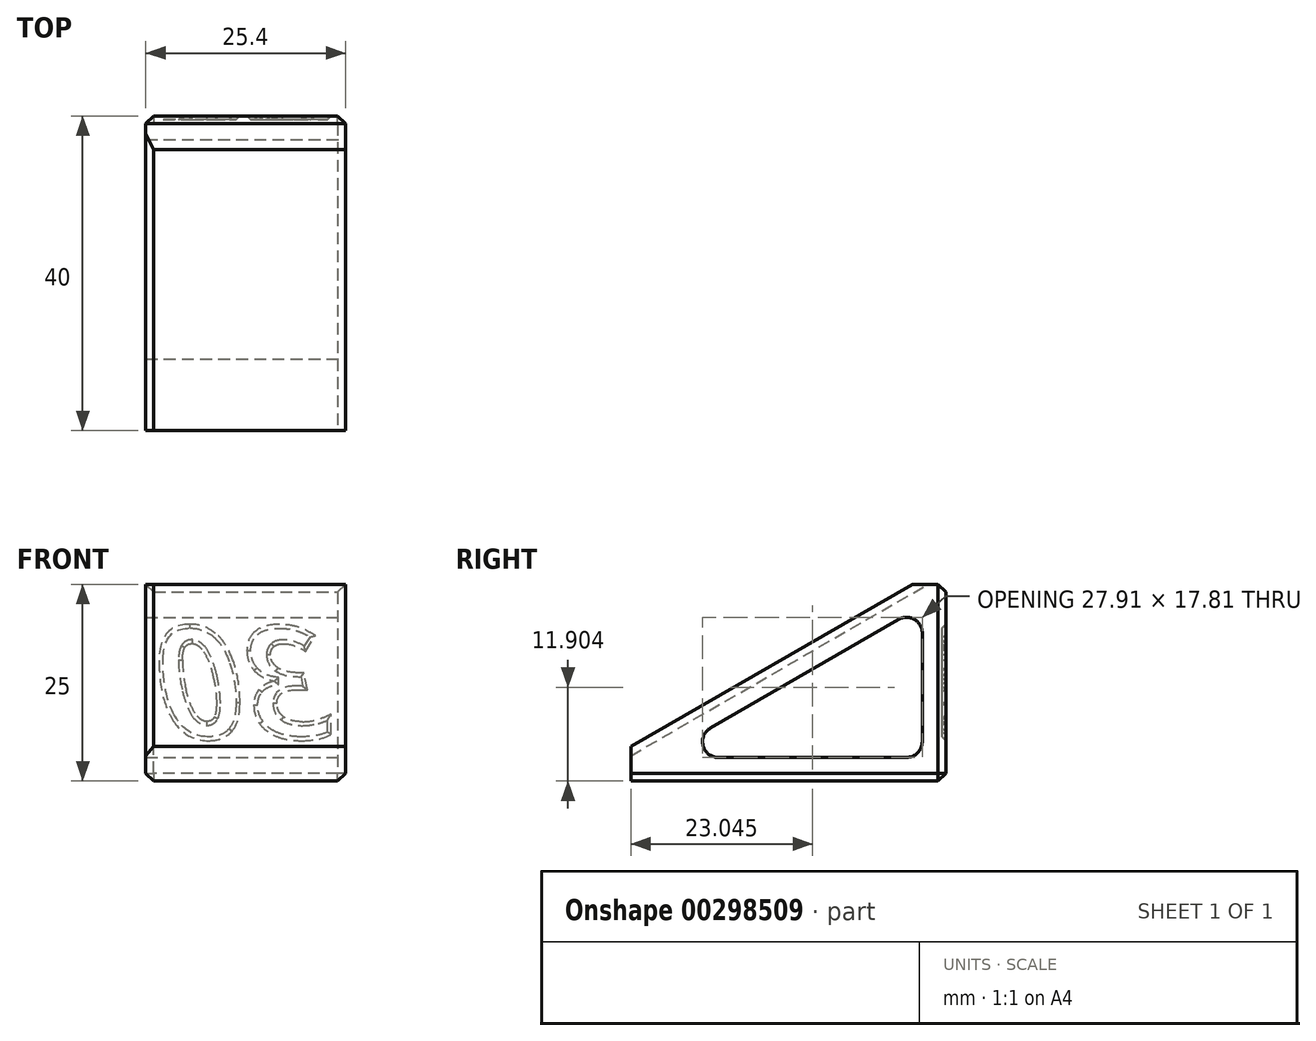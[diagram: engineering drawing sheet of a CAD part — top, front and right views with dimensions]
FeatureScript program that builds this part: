
annotation { "Feature Type Name" : "Feature", "Feature Type Description" : "" }
export const myFeature = defineFeature(function(context is Context, id is Id, definition is map)
    precondition{}
    {
        {
            var Q0;
            Q0=qCreatedBy(makeId("Top.planeOp"),FACE);
            var sketch = newSketch(context, id + "F0", { "sketchPlane" : qUnion([Q0])});
            skLineSegment(sketch, "E0.rect.bottom", {"start": v(-12.7, 20) * mm, "end": v(12.7, 20) * mm});
            skLineSegment(sketch, "E0.rect.top", {"start": v(-12.7, -20) * mm, "end": v(12.7, -20) * mm});
            skLineSegment(sketch, "E0.rect.left", {"start": v(-12.7, 20) * mm, "end": v(-12.7, -20) * mm});
            skLineSegment(sketch, "E0.rect.right", {"start": v(12.7, 20) * mm, "end": v(12.7, -20) * mm});
            skPoint(sketch, "E0.rect.middle", {"position": v(0, 0) * mm});
            skSolve(sketch);
        }
        {
            var Q0;
            Q0=qSketchRegion(id+"F0",true);
            extrude(context, id + "F1", {"entities" : qUnion([Q0]), "depth" : 25 * mm});
        }
        {
            var Q0;
            Q0=makeQuery(id+"F1.opExtrude","SWEPT_FACE",FACE,{"disambiguationData":[OSD([sQuery(id+"F0.wireOp",EDGE,"E0.rect.right")])]});
            var sketch = newSketch(context, id + "F2", { "sketchPlane" : qUnion([Q0])});
            skLineSegment(sketch, "E1", {"start": v(20, 27.47) * mm, "end": v(-20, 4.37) * mm});
            skLineSegment(sketch, "E2", {"start": v(-20, 0) * mm, "end": v(-20, 36.1) * mm});
            skLineSegment(sketch, "E3", {"start": v(-20, 36.1) * mm, "end": v(20, 36.1) * mm});
            skLineSegment(sketch, "E4", {"start": v(20, 36.1) * mm, "end": v(20, 27.47) * mm});
            skSolve(sketch);
        }
        {
            var Q0;
            Q0=qSketchRegion(id+"F2",true);
            extrude(context, id + "F3", {"entities" : qUnion([Q0]), "operationType" : NewBodyOperationType.REMOVE, "endBound" : BoundingType.THROUGH_ALL, "oppositeDirection" : true, "depth" : 25 * mm});
        }
        {
            var Q0;
            Q0=makeQuery(id+"F1.opExtrude","SWEPT_FACE",FACE,{"disambiguationData":[OSD([sQuery(id+"F0.wireOp",EDGE,"E0.rect.right")])]});
            var sketch = newSketch(context, id + "F4", { "sketchPlane" : qUnion([Q0])});
            skLineSegment(sketch, "E5.0", {"start": v(12, 3) * mm, "end": v(-16.38, 3) * mm});
            skLineSegment(sketch, "E5.1", {"start": v(13.5, 20.25) * mm, "end": v(-16.38, 3) * mm});
            skLineSegment(sketch, "E5.2", {"start": v(17, 3) * mm, "end": v(12, 3) * mm});
            skLineSegment(sketch, "E5.3", {"start": v(17, 22.27) * mm, "end": v(17, 3) * mm});
            skLineSegment(sketch, "E5.4", {"start": v(17, 22.27) * mm, "end": v(13.5, 20.25) * mm});
            skSolve(sketch);
        }
        {
            var Q0;
            Q0=qSketchRegion(id+"F4",true);
            extrude(context, id + "F5", {"entities" : qUnion([Q0]), "operationType" : NewBodyOperationType.REMOVE, "endBound" : BoundingType.THROUGH_ALL, "oppositeDirection" : true, "depth" : 25 * mm});
        }
        {
            var Q0;
            Q0=makeQuery(id+"F5.boolean.opBoolean","COPY",EDGE,{"derivedFrom":makeQuery(id+"F5.opExtrude","SWEPT_EDGE",EDGE,{"disambiguationData":[OSD([sQuery(id+"F4.wireOp",EDGE,"E5.3"),sQuery(id+"F4.wireOp",EDGE,"E5.4")])]})});
            var Q1;
            Q1=makeQuery(id+"F5.boolean.opBoolean","COPY",EDGE,{"derivedFrom":makeQuery(id+"F5.opExtrude","SWEPT_EDGE",EDGE,{"disambiguationData":[OSD([sQuery(id+"F4.wireOp",EDGE,"E5.0"),sQuery(id+"F4.wireOp",EDGE,"E5.1")])]})});
            var Q2;
            Q2=makeQuery(id+"F5.boolean.opBoolean","COPY",EDGE,{"derivedFrom":makeQuery(id+"F5.opExtrude","SWEPT_EDGE",EDGE,{"disambiguationData":[OSD([sQuery(id+"F4.wireOp",EDGE,"E5.2"),sQuery(id+"F4.wireOp",EDGE,"E5.3")])]})});
            fillet(context, id + "F6", {"entities" : qUnion([Q0, Q1, Q2]), "radius" : 2 * mm, "tangentPropagation" : true, "allowEdgeOverflow" : false});
        }
        {
            var Q0;
            Q0=makeQuery(id+"F1.opExtrude","SWEPT_FACE",FACE,{"disambiguationData":[OSD([sQuery(id+"F0.wireOp",EDGE,"E0.rect.bottom")])]});
            var sketch = newSketch(context, id + "F7", { "sketchPlane" : qUnion([Q0])});
            skText(sketch, "E6", { "text": "30", "fontName": "OpenSans-BoldItalic.ttf"});
            const initialGuessF7  = {"E6": [-0.011, 0.00532, 1, 0, 0.0145]};
            skSetInitialGuess(sketch, initialGuessF7);
            skSolve(sketch);
        }
        {
            var Q0;
            Q0=qSketchRegion(id+"F7",true);
            extrude(context, id + "F8", {"entities" : qUnion([Q0]), "operationType" : NewBodyOperationType.REMOVE, "oppositeDirection" : true, "depth" : .5 * mm});
        }
        {
            var Q0;
            Q0=makeQuery(id+"F8.boolean.opBoolean","COPY",FACE,{"derivedFrom":makeQuery(id+"F8.opExtrude","CAP_FACE",FACE,{"disambiguationData":[OSD([sQuery(id+"F7.wireOp",EDGE,"E6.sketch_text.stroke-0"),sQuery(id+"F7.wireOp",EDGE,"E6.sketch_text.stroke-1"),sQuery(id+"F7.wireOp",EDGE,"E6.sketch_text.stroke-2"),sQuery(id+"F7.wireOp",EDGE,"E6.sketch_text.stroke-3"),sQuery(id+"F7.wireOp",EDGE,"E6.sketch_text.stroke-4"),sQuery(id+"F7.wireOp",EDGE,"E6.sketch_text.stroke-5"),sQuery(id+"F7.wireOp",EDGE,"E6.sketch_text.stroke-6"),sQuery(id+"F7.wireOp",EDGE,"E6.sketch_text.stroke-7"),sQuery(id+"F7.wireOp",EDGE,"E6.sketch_text.stroke-8"),sQuery(id+"F7.wireOp",EDGE,"E6.sketch_text.stroke-9"),sQuery(id+"F7.wireOp",EDGE,"E6.sketch_text.stroke-10"),sQuery(id+"F7.wireOp",EDGE,"E6.sketch_text.stroke-11"),sQuery(id+"F7.wireOp",EDGE,"E6.sketch_text.stroke-12"),sQuery(id+"F7.wireOp",EDGE,"E6.sketch_text.stroke-13"),sQuery(id+"F7.wireOp",EDGE,"E6.sketch_text.stroke-14"),sQuery(id+"F7.wireOp",EDGE,"E6.sketch_text.stroke-15"),sQuery(id+"F7.wireOp",EDGE,"E6.sketch_text.stroke-16"),sQuery(id+"F7.wireOp",EDGE,"E6.sketch_text.stroke-17"),sQuery(id+"F7.wireOp",EDGE,"E6.sketch_text.stroke-18"),sQuery(id+"F7.wireOp",EDGE,"E6.sketch_text.stroke-19"),sQuery(id+"F7.wireOp",EDGE,"E6.sketch_text.stroke-20"),sQuery(id+"F7.wireOp",EDGE,"E6.sketch_text.stroke-21"),sQuery(id+"F7.wireOp",EDGE,"E6.sketch_text.stroke-22"),sQuery(id+"F7.wireOp",EDGE,"E6.sketch_text.stroke-23"),sQuery(id+"F7.wireOp",EDGE,"E6.sketch_text.stroke-24"),sQuery(id+"F7.wireOp",EDGE,"E6.sketch_text.stroke-25"),sQuery(id+"F7.wireOp",EDGE,"E6.sketch_text.stroke-26"),sQuery(id+"F7.wireOp",EDGE,"E6.sketch_text.stroke-27")])],"isStart":false})});
            var Q1;
            Q1=makeQuery(id+"F8.boolean.opBoolean","COPY",FACE,{"derivedFrom":makeQuery(id+"F8.opExtrude","CAP_FACE",FACE,{"disambiguationData":[OSD([sQuery(id+"F7.wireOp",EDGE,"E6.sketch_text.stroke-28"),sQuery(id+"F7.wireOp",EDGE,"E6.sketch_text.stroke-29"),sQuery(id+"F7.wireOp",EDGE,"E6.sketch_text.stroke-30"),sQuery(id+"F7.wireOp",EDGE,"E6.sketch_text.stroke-31"),sQuery(id+"F7.wireOp",EDGE,"E6.sketch_text.stroke-32"),sQuery(id+"F7.wireOp",EDGE,"E6.sketch_text.stroke-33"),sQuery(id+"F7.wireOp",EDGE,"E6.sketch_text.stroke-34"),sQuery(id+"F7.wireOp",EDGE,"E6.sketch_text.stroke-35"),sQuery(id+"F7.wireOp",EDGE,"E6.sketch_text.stroke-36"),sQuery(id+"F7.wireOp",EDGE,"E6.sketch_text.stroke-37"),sQuery(id+"F7.wireOp",EDGE,"E6.sketch_text.stroke-38"),sQuery(id+"F7.wireOp",EDGE,"E6.sketch_text.stroke-39"),sQuery(id+"F7.wireOp",EDGE,"E6.sketch_text.stroke-40"),sQuery(id+"F7.wireOp",EDGE,"E6.sketch_text.stroke-41"),sQuery(id+"F7.wireOp",EDGE,"E6.sketch_text.stroke-42"),sQuery(id+"F7.wireOp",EDGE,"E6.sketch_text.stroke-43"),sQuery(id+"F7.wireOp",EDGE,"E6.sketch_text.stroke-44"),sQuery(id+"F7.wireOp",EDGE,"E6.sketch_text.stroke-45")])],"isStart":false})});
            chamfer(context, id + "F9", {"entities" : qUnion([Q0, Q1]), "width" : .5 * mm, "tangentPropagation" : true});
        }
        {
            var Q0;
            Q0=makeQuery(id+"F1.opExtrude","SWEPT_EDGE",EDGE,{"disambiguationData":[OSD([sQuery(id+"F0.wireOp",EDGE,"E0.rect.bottom"),sQuery(id+"F0.wireOp",EDGE,"E0.rect.right")])]});
            var Q1;
            Q1=makeQuery(id+"F1.opExtrude","CAP_EDGE",EDGE,{"disambiguationData":[OSD([sQuery(id+"F0.wireOp",EDGE,"E0.rect.bottom")])],"isStart":false});
            var Q2;
            Q2=makeQuery(id+"F1.opExtrude","SWEPT_EDGE",EDGE,{"disambiguationData":[OSD([sQuery(id+"F0.wireOp",EDGE,"E0.rect.bottom"),sQuery(id+"F0.wireOp",EDGE,"E0.rect.left")])]});
            var Q3;
            Q3=makeQuery(id+"F1.opExtrude","CAP_EDGE",EDGE,{"disambiguationData":[OSD([sQuery(id+"F0.wireOp",EDGE,"E0.rect.bottom")])],"isStart":true});
            var Q4;
            Q4=makeQuery(id+"F1.opExtrude","CAP_EDGE",EDGE,{"disambiguationData":[OSD([sQuery(id+"F0.wireOp",EDGE,"E0.rect.right")])],"isStart":true});
            var Q5;
            Q5=makeQuery(id+"F1.opExtrude","CAP_EDGE",EDGE,{"disambiguationData":[OSD([sQuery(id+"F0.wireOp",EDGE,"E0.rect.left")])],"isStart":true});
            var Q6;
            Q6=makeQuery(id+"F3.boolean.opBoolean","COPY",EDGE,{"derivedFrom":makeQuery(id+"F3.opExtrude","CAP_EDGE",EDGE,{"disambiguationData":[OSD([sQuery(id+"F2.wireOp",EDGE,"E1")])],"isStart":true})});
            var Q7;
            Q7=makeQuery(id+"F3.boolean.opBoolean","INTERSECT",EDGE,{"derivedFrom":[makeQuery(id+"F1.opExtrude","SWEPT_FACE",FACE,{"disambiguationData":[OSD([sQuery(id+"F0.wireOp",EDGE,"E0.rect.left")])]}),makeQuery(id+"F3.opExtrude","SWEPT_FACE",FACE,{"disambiguationData":[OSD([sQuery(id+"F2.wireOp",EDGE,"E1")])]})]});
            chamfer(context, id + "F10", {"entities" : qUnion([Q0, Q1, Q2, Q3, Q4, Q5, Q6, Q7]), "width" : 1 * mm, "tangentPropagation" : true});
        }
    });
